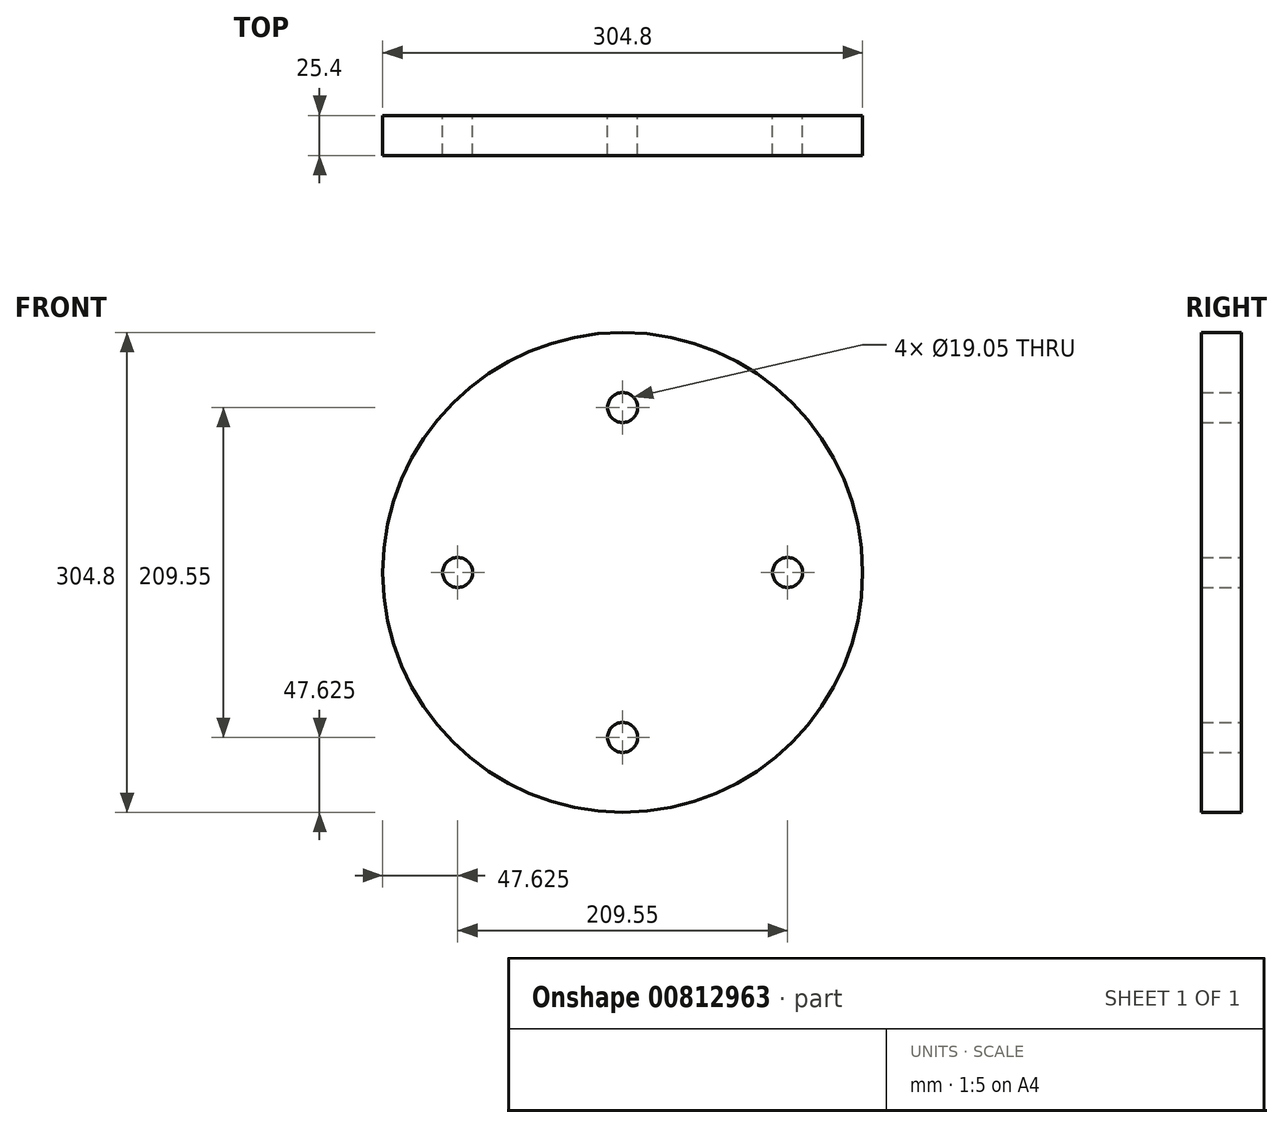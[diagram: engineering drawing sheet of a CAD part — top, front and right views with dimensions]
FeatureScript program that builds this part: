
annotation { "Feature Type Name" : "Feature", "Feature Type Description" : "" }
export const myFeature = defineFeature(function(context is Context, id is Id, definition is map)
    precondition{}
    {
        {
            var Q0;
            Q0=qCreatedBy(makeId("Front.planeOp"),FACE);
            var sketch = newSketch(context, id + "F0", { "sketchPlane" : qUnion([Q0])});
            skCircle(sketch, "E0", {"center": v(0, 0) * mm, "radius": 152.4 * mm});
            skLineSegment(sketch, "E1", {"start": v(0, 246.57) * mm, "end": v(0, -248.45) * mm, "construction": true});
            skLineSegment(sketch, "E2", {"start": v(464.21, 0) * mm, "end": v(-516.63, 0) * mm, "construction": true});
            skCircle(sketch, "E3", {"center": v(0, 104.78) * mm, "radius": 9.53 * mm});
            skCircle(sketch, "E4", {"center": v(-104.78, 0) * mm, "radius": 9.53 * mm});
            skCircle(sketch, "E5", {"center": v(104.78, 0) * mm, "radius": 9.53 * mm});
            skCircle(sketch, "E6", {"center": v(0, -104.78) * mm, "radius": 9.53 * mm});
            skSolve(sketch);
        }
        {
            var Q0;
            Q0 = qSketchRegion(id + "F0", true);
            extrude(context, id + "F1", {"entities" : qUnion([Q0]), "depth" : 25.4 * mm, "offsetDistance" : 25.4 * mm});
        }
    });
